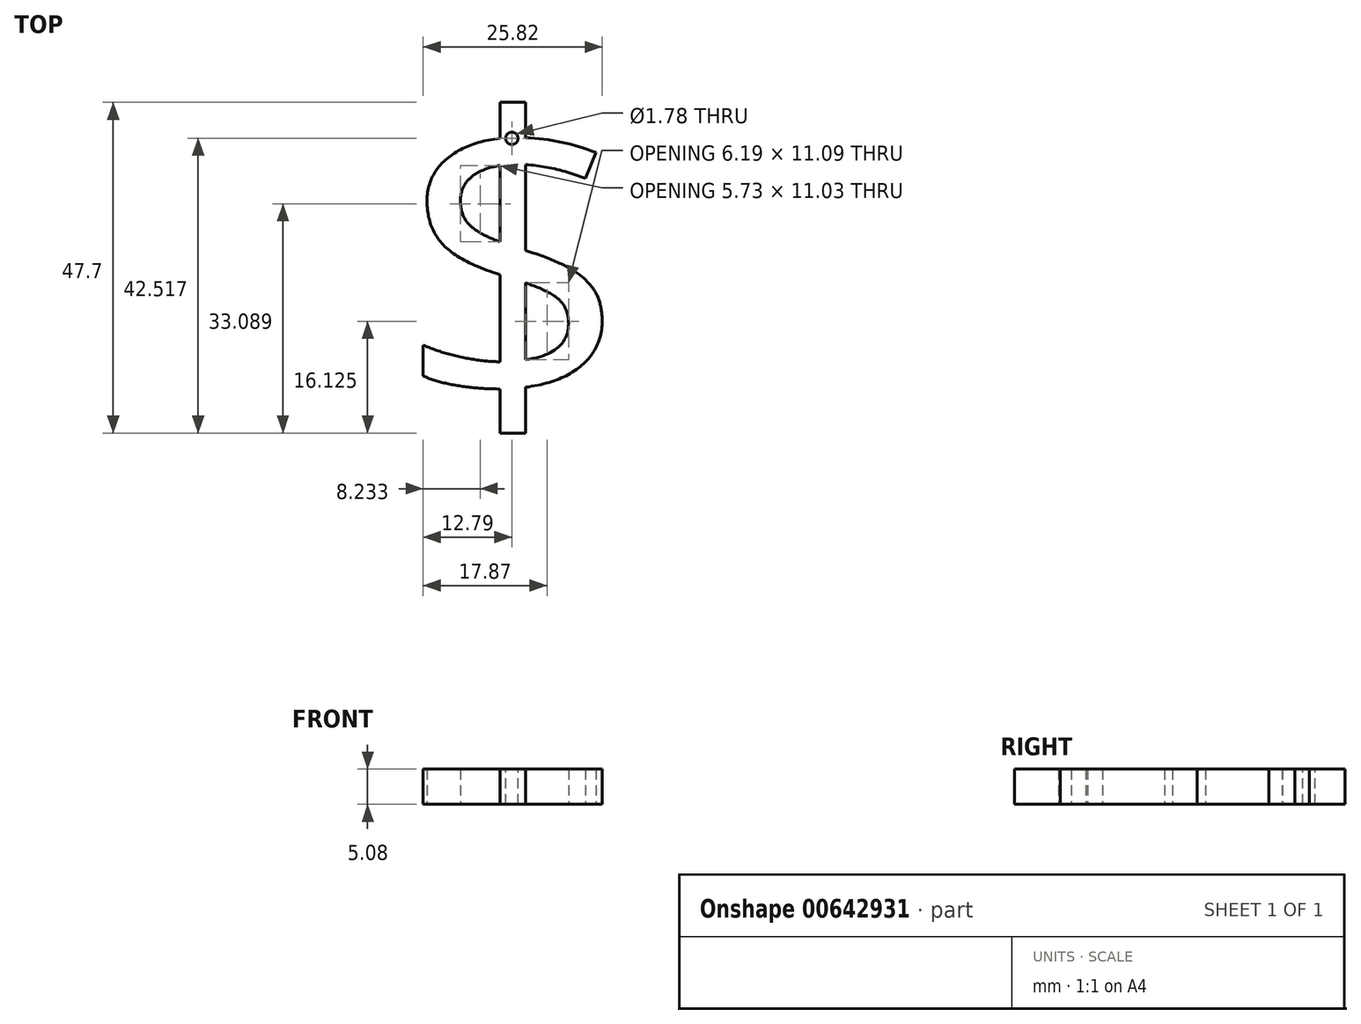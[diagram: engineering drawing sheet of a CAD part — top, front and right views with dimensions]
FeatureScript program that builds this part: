
annotation { "Feature Type Name" : "Feature", "Feature Type Description" : "" }
export const myFeature = defineFeature(function(context is Context, id is Id, definition is map)
    precondition{}
    {
        {
            var Q0;
            Q0=qCreatedBy(makeId("Top.planeOp"),FACE);
            var sketch = newSketch(context, id + "F0", { "sketchPlane" : qUnion([Q0])});
            skText(sketch, "E0", { "text": "$", "fontName": "OpenSans-Regular.ttf"});
            const initialGuessF0  = {"E0": [-0.03333, 0, 1, 0, 0.04205]};
            skSetInitialGuess(sketch, initialGuessF0);
            skSolve(sketch);
        }
        {
            var Q0;
            Q0 = qSketchRegion(id + "F0", true);
            extrude(context, id + "F1", {"entities" : qUnion([Q0]), "depth" : 5.08 * mm, "offsetDistance" : 25.4 * mm});
        }
        {
            var Q0;
            Q0=makeQuery(id+"F1.opExtrude","CAP_FACE",FACE,{"disambiguationData":[OSD([sQuery(id+"F0.wireOp",EDGE,"E0.sketch_text.stroke-0"),sQuery(id+"F0.wireOp",EDGE,"E0.sketch_text.stroke-1"),sQuery(id+"F0.wireOp",EDGE,"E0.sketch_text.stroke-2"),sQuery(id+"F0.wireOp",EDGE,"E0.sketch_text.stroke-3"),sQuery(id+"F0.wireOp",EDGE,"E0.sketch_text.stroke-4"),sQuery(id+"F0.wireOp",EDGE,"E0.sketch_text.stroke-5"),sQuery(id+"F0.wireOp",EDGE,"E0.sketch_text.stroke-6"),sQuery(id+"F0.wireOp",EDGE,"E0.sketch_text.stroke-7"),sQuery(id+"F0.wireOp",EDGE,"E0.sketch_text.stroke-8"),sQuery(id+"F0.wireOp",EDGE,"E0.sketch_text.stroke-9"),sQuery(id+"F0.wireOp",EDGE,"E0.sketch_text.stroke-10"),sQuery(id+"F0.wireOp",EDGE,"E0.sketch_text.stroke-11"),sQuery(id+"F0.wireOp",EDGE,"E0.sketch_text.stroke-12"),sQuery(id+"F0.wireOp",EDGE,"E0.sketch_text.stroke-13"),sQuery(id+"F0.wireOp",EDGE,"E0.sketch_text.stroke-14"),sQuery(id+"F0.wireOp",EDGE,"E0.sketch_text.stroke-15"),sQuery(id+"F0.wireOp",EDGE,"E0.sketch_text.stroke-16"),sQuery(id+"F0.wireOp",EDGE,"E0.sketch_text.stroke-17"),sQuery(id+"F0.wireOp",EDGE,"E0.sketch_text.stroke-18"),sQuery(id+"F0.wireOp",EDGE,"E0.sketch_text.stroke-19"),sQuery(id+"F0.wireOp",EDGE,"E0.sketch_text.stroke-20"),sQuery(id+"F0.wireOp",EDGE,"E0.sketch_text.stroke-21"),sQuery(id+"F0.wireOp",EDGE,"E0.sketch_text.stroke-22"),sQuery(id+"F0.wireOp",EDGE,"E0.sketch_text.stroke-23"),sQuery(id+"F0.wireOp",EDGE,"E0.sketch_text.stroke-24"),sQuery(id+"F0.wireOp",EDGE,"E0.sketch_text.stroke-25"),sQuery(id+"F0.wireOp",EDGE,"E0.sketch_text.stroke-26"),sQuery(id+"F0.wireOp",EDGE,"E0.sketch_text.stroke-27"),sQuery(id+"F0.wireOp",EDGE,"E0.sketch_text.stroke-28"),sQuery(id+"F0.wireOp",EDGE,"E0.sketch_text.stroke-29"),sQuery(id+"F0.wireOp",EDGE,"E0.sketch_text.stroke-30"),sQuery(id+"F0.wireOp",EDGE,"E0.sketch_text.stroke-31"),sQuery(id+"F0.wireOp",EDGE,"E0.sketch_text.stroke-32"),sQuery(id+"F0.wireOp",EDGE,"E0.sketch_text.stroke-33")])],"isStart":false});
            var sketch = newSketch(context, id + "F2", { "sketchPlane" : qUnion([Q0])});
            skCircle(sketch, "E1", {"center": v(-16.81, 39.13) * mm, "radius": 0.89 * mm});
            skSolve(sketch);
        }
        {
            var Q0;
            Q0 = qSketchRegion(id + "F2", true);
            extrude(context, id + "F3", {"entities" : qUnion([Q0]), "operationType" : NewBodyOperationType.REMOVE, "oppositeDirection" : true, "depth" : 5.08 * mm, "offsetDistance" : 25.4 * mm});
        }
    });
